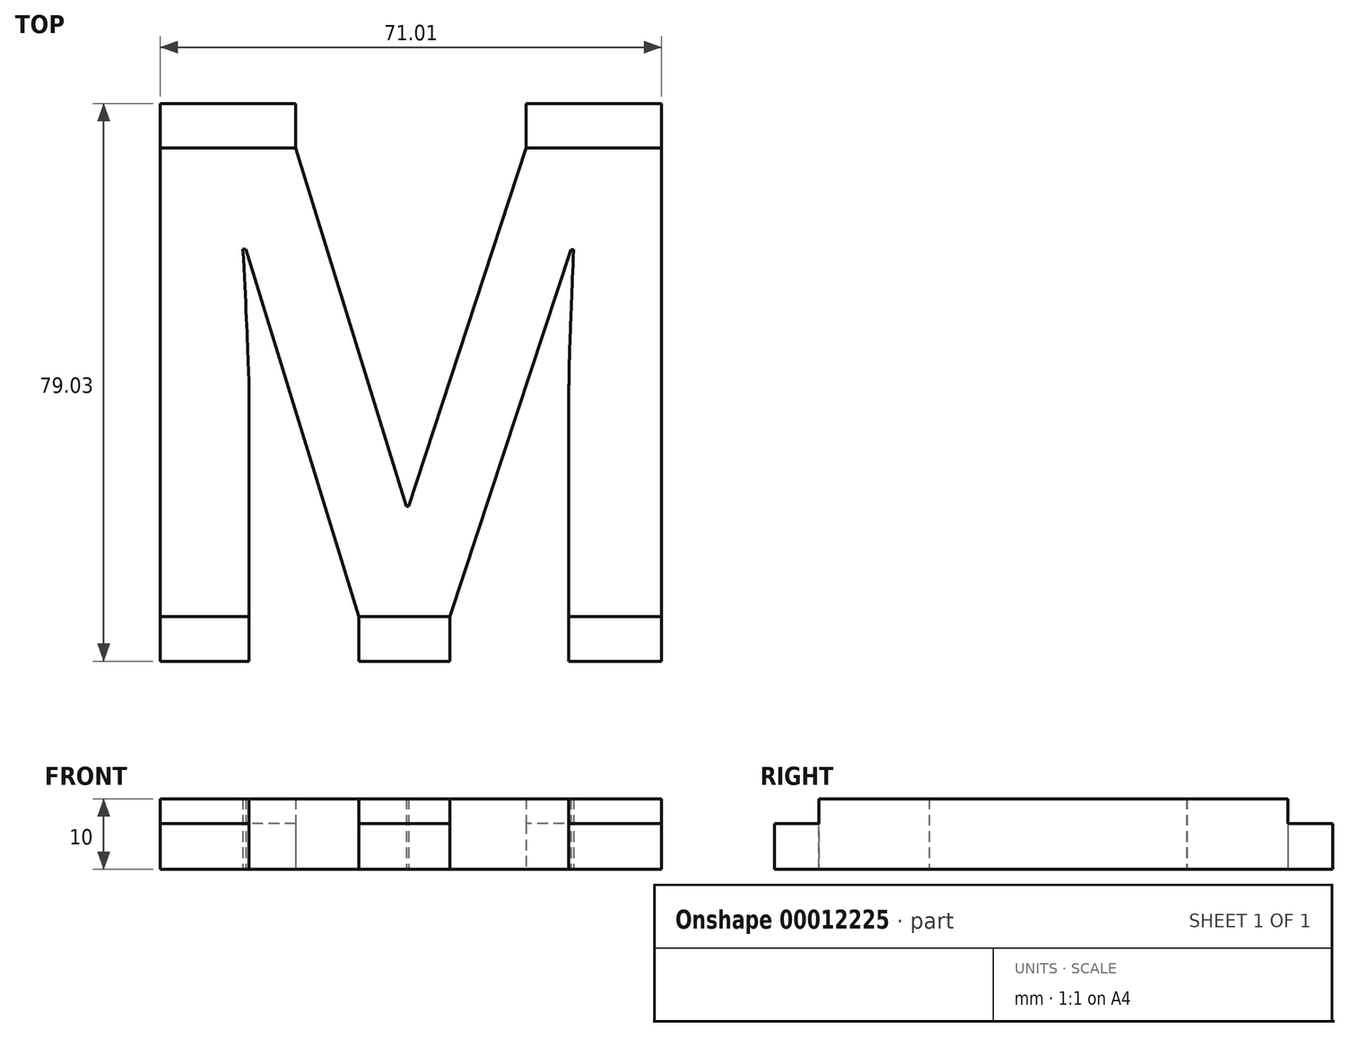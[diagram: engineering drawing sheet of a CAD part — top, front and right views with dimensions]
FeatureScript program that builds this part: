
annotation { "Feature Type Name" : "Feature", "Feature Type Description" : "" }
export const myFeature = defineFeature(function(context is Context, id is Id, definition is map)
    precondition{}
    {
        {
            var Q0;
            Q0=qCreatedBy(makeId("Top.planeOp"),FACE);
            var sketch = newSketch(context, id + "F0", { "sketchPlane" : qUnion([Q0])});
            skText(sketch, "E0", { "text": "M", "fontName": "OpenSans-Bold.ttf"});
            const initialGuessF0  = {"E0": [-0.07937, 0, 1, 0, 0.067]};
            skSetInitialGuess(sketch, initialGuessF0);
            skSolve(sketch);
        }
        {
            var Q0;
            Q0=makeQuery(id+"F0.imprint","IMPRINT",FACE,{"disambiguationData":[TD([[makeQuery(id+"F0.imprint","IMPRINT",EDGE,{"derivedFrom":sQuery(id+"F0.wireOp",EDGE,"E0.sketch_text.stroke-0")}),-1.0]])]});
            extrude(context, id + "F1", {"entities" : qUnion([Q0]), "depth" : 10 * mm});
        }
        {
            var Q0;
            Q0=makeQuery(id+"F1.opExtrude","SWEPT_FACE",FACE,{"disambiguationData":[OSD([sQuery(id+"F0.wireOp",EDGE,"E0.sketch_text.stroke-10")])]});
            var sketch = newSketch(context, id + "F2", { "sketchPlane" : qUnion([Q0])});
            skLineSegment(sketch, "E1.0.0", {"start": v(0, 0) * mm, "end": v(19.16, 0) * mm});
            skLineSegment(sketch, "E1.0.1", {"start": v(19.16, 0) * mm, "end": v(19.16, 10) * mm});
            skLineSegment(sketch, "E1.0.2", {"start": v(19.16, 10) * mm, "end": v(0, 10) * mm});
            skLineSegment(sketch, "E1.0.3", {"start": v(0, 10) * mm, "end": v(0, 0) * mm});
            skLineSegment(sketch, "E2.top", {"start": v(0, 6.5) * mm, "end": v(19.16, 6.5) * mm});
            skLineSegment(sketch, "E2.left", {"start": v(0, 0) * mm, "end": v(0, 6.5) * mm});
            skLineSegment(sketch, "E2.right", {"start": v(19.16, 0) * mm, "end": v(19.16, 6.5) * mm});
            skLineSegment(sketch, "E3.0.0", {"start": v(51.83, 0) * mm, "end": v(71.01, 0) * mm});
            skLineSegment(sketch, "E3.0.1", {"start": v(71.01, 0) * mm, "end": v(71.01, 10) * mm});
            skLineSegment(sketch, "E3.0.2", {"start": v(71.01, 10) * mm, "end": v(51.83, 10) * mm});
            skLineSegment(sketch, "E3.0.3", {"start": v(51.83, 10) * mm, "end": v(51.83, 0) * mm});
            skLineSegment(sketch, "E4.top", {"start": v(51.83, 6.5) * mm, "end": v(71.01, 6.5) * mm});
            skLineSegment(sketch, "E4.left", {"start": v(51.83, 0) * mm, "end": v(51.83, 6.5) * mm});
            skLineSegment(sketch, "E4.right", {"start": v(71.01, 0) * mm, "end": v(71.01, 6.5) * mm});
            skSolve(sketch);
        }
        {
            var Q0;
            Q0=makeQuery(id+"F2.imprint","IMPRINT",FACE,{"disambiguationData":[TD([[makeQuery(id+"F2.imprint","IMPRINT",EDGE,{"derivedFrom":sQuery(id+"F2.wireOp",EDGE,"E1.0.0")}),-1.0]])]});
            var Q1;
            Q1=makeQuery(id+"F2.imprint","IMPRINT",FACE,{"disambiguationData":[TD([[makeQuery(id+"F2.imprint","IMPRINT",EDGE,{"derivedFrom":sQuery(id+"F2.wireOp",EDGE,"E3.0.0")}),1.0]])]});
            extrude(context, id + "F3", {"entities" : qUnion([Q0, Q1]), "operationType" : NewBodyOperationType.ADD, "depth" : 6.3 * mm});
        }
        {
            var Q0;
            Q0=makeQuery(id+"F1.opExtrude","SWEPT_FACE",FACE,{"disambiguationData":[OSD([sQuery(id+"F0.wireOp",EDGE,"E0.sketch_text.stroke-4")])]});
            var sketch = newSketch(context, id + "F4", { "sketchPlane" : qUnion([Q0])});
            skLineSegment(sketch, "E5.0.0", {"start": v(-71.01, 0) * mm, "end": v(-58.42, 0) * mm});
            skLineSegment(sketch, "E5.0.1", {"start": v(-58.42, 0) * mm, "end": v(-58.42, 10) * mm});
            skLineSegment(sketch, "E5.0.2", {"start": v(-58.42, 10) * mm, "end": v(-71.01, 10) * mm});
            skLineSegment(sketch, "E5.0.3", {"start": v(-71.01, 10) * mm, "end": v(-71.01, 0) * mm});
            skLineSegment(sketch, "E6.0.0", {"start": v(-42.9, 0) * mm, "end": v(-29.98, 0) * mm});
            skLineSegment(sketch, "E6.0.1", {"start": v(-29.98, 0) * mm, "end": v(-29.98, 10) * mm});
            skLineSegment(sketch, "E6.0.2", {"start": v(-29.98, 10) * mm, "end": v(-42.9, 10) * mm});
            skLineSegment(sketch, "E6.0.3", {"start": v(-42.9, 10) * mm, "end": v(-42.9, 0) * mm});
            skLineSegment(sketch, "E7.0.0", {"start": v(-13.13, 0) * mm, "end": v(0, 0) * mm});
            skLineSegment(sketch, "E7.0.1", {"start": v(0, 0) * mm, "end": v(0, 10) * mm});
            skLineSegment(sketch, "E7.0.2", {"start": v(0, 10) * mm, "end": v(-13.13, 10) * mm});
            skLineSegment(sketch, "E7.0.3", {"start": v(-13.13, 10) * mm, "end": v(-13.13, 0) * mm});
            skLineSegment(sketch, "E8.top", {"start": v(-71.01, 6.5) * mm, "end": v(-58.42, 6.5) * mm});
            skLineSegment(sketch, "E8.left", {"start": v(-71.01, 0) * mm, "end": v(-71.01, 6.5) * mm});
            skLineSegment(sketch, "E8.right", {"start": v(-58.42, 0) * mm, "end": v(-58.42, 6.5) * mm});
            skLineSegment(sketch, "E9.top", {"start": v(-42.9, 6.5) * mm, "end": v(-29.98, 6.5) * mm});
            skLineSegment(sketch, "E9.left", {"start": v(-42.9, 0) * mm, "end": v(-42.9, 6.5) * mm});
            skLineSegment(sketch, "E9.right", {"start": v(-29.98, 0) * mm, "end": v(-29.98, 6.5) * mm});
            skLineSegment(sketch, "E10.top", {"start": v(-13.13, 6.5) * mm, "end": v(0, 6.5) * mm});
            skLineSegment(sketch, "E10.left", {"start": v(-13.13, 0) * mm, "end": v(-13.13, 6.5) * mm});
            skLineSegment(sketch, "E10.right", {"start": v(0, 0) * mm, "end": v(0, 6.5) * mm});
            skSolve(sketch);
        }
        {
            var Q0;
            Q0=makeQuery(id+"F4.imprint","IMPRINT",FACE,{"disambiguationData":[TD([[makeQuery(id+"F4.imprint","IMPRINT",EDGE,{"derivedFrom":sQuery(id+"F4.wireOp",EDGE,"E5.0.0")}),-1.0]])]});
            var Q1;
            Q1=makeQuery(id+"F4.imprint","IMPRINT",FACE,{"disambiguationData":[TD([[makeQuery(id+"F4.imprint","IMPRINT",EDGE,{"derivedFrom":sQuery(id+"F4.wireOp",EDGE,"E6.0.0")}),1.0]])]});
            var Q2;
            Q2=makeQuery(id+"F4.imprint","IMPRINT",FACE,{"disambiguationData":[TD([[makeQuery(id+"F4.imprint","IMPRINT",EDGE,{"derivedFrom":sQuery(id+"F4.wireOp",EDGE,"E7.0.0")}),1.0]])]});
            extrude(context, id + "F5", {"entities" : qUnion([Q0, Q1, Q2]), "operationType" : NewBodyOperationType.ADD, "depth" : 6.3 * mm});
        }
    });
